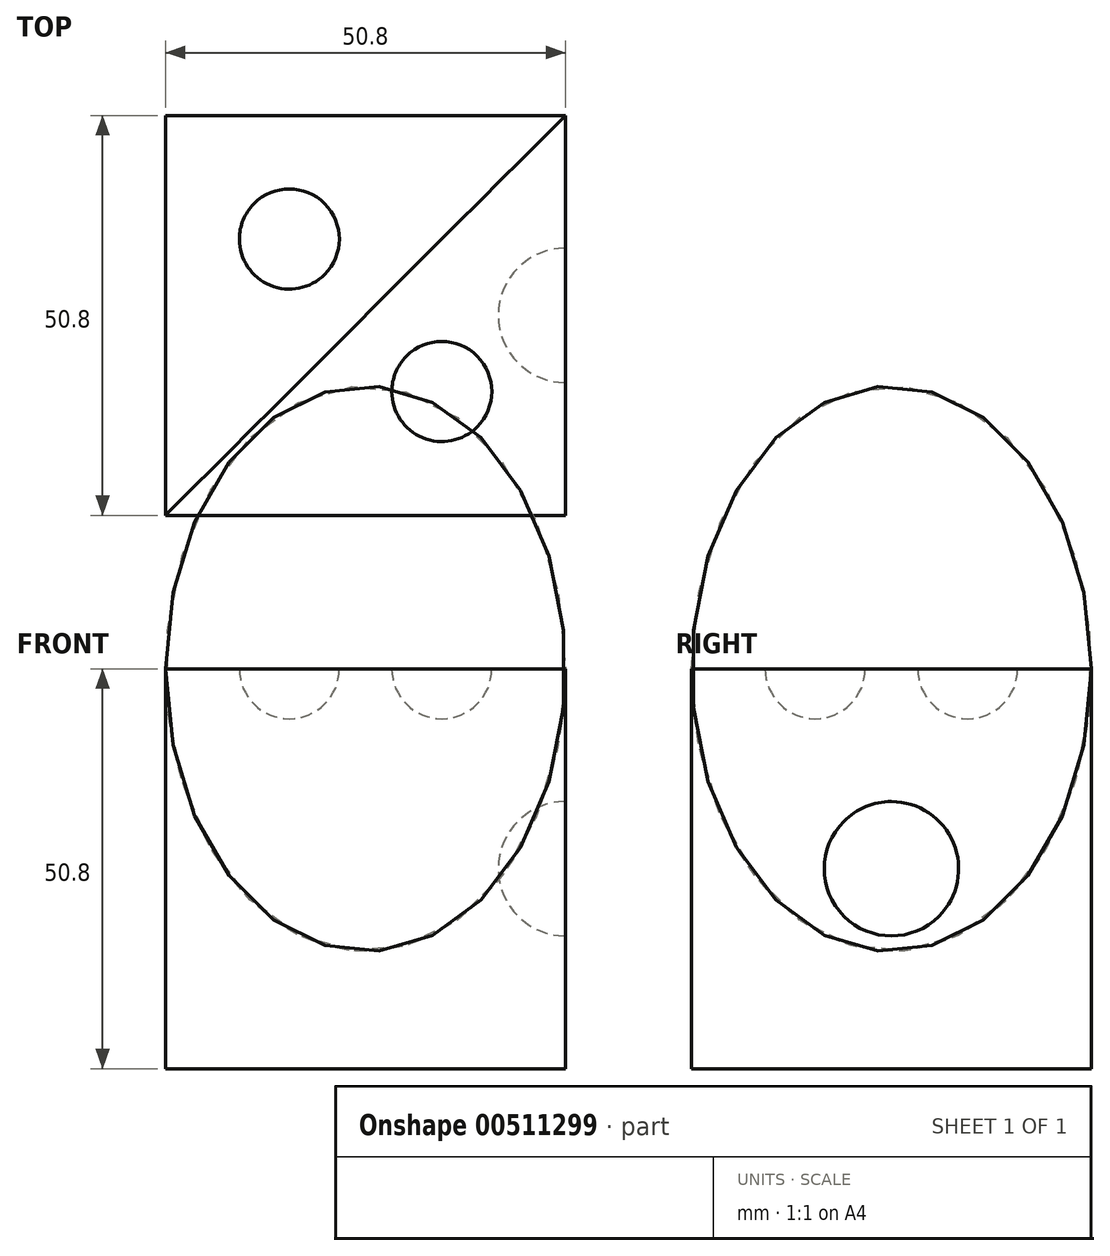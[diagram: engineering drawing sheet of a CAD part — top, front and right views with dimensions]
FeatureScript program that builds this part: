
annotation { "Feature Type Name" : "Feature", "Feature Type Description" : "" }
export const myFeature = defineFeature(function(context is Context, id is Id, definition is map)
    precondition{}
    {
        {
            var Q0;
            Q0=qCreatedBy(makeId("Front.planeOp"),FACE);
            var sketch = newSketch(context, id + "F0", { "sketchPlane" : qUnion([Q0])});
            skLineSegment(sketch, "E0", {"start": v(0, 0) * mm, "end": v(0, 50.8) * mm});
            skLineSegment(sketch, "E1", {"start": v(0, 0) * mm, "end": v(-50.8, 0) * mm});
            skLineSegment(sketch, "E2", {"start": v(0, 50.8) * mm, "end": v(-50.8, 50.8) * mm});
            skLineSegment(sketch, "E3", {"start": v(-50.8, 50.8) * mm, "end": v(-50.8, 0) * mm});
            skSolve(sketch);
        }
        {
            var Q0;
            Q0=makeQuery(id+"F0.imprint","IMPRINT",FACE,{"disambiguationData":[TD([[makeQuery(id+"F0.imprint","IMPRINT",EDGE,{"derivedFrom":sQuery(id+"F0.wireOp",EDGE,"E0")}),1.0]])]});
            extrude(context, id + "F1", {"entities" : qUnion([Q0]), "depth" : 50.8 * mm, "offsetDistance" : 25.4 * mm});
        }
        {
            var Q0;
            Q0=makeQuery(id+"F1.opExtrude","SWEPT_FACE",FACE,{"disambiguationData":[OSD([sQuery(id+"F0.wireOp",EDGE,"E0")])]});
            var sketch = newSketch(context, id + "F2", { "sketchPlane" : qUnion([Q0])});
            skCircle(sketch, "E4", {"center": v(-25.4, 25.4) * mm, "radius": 8.54 * mm});
            skPoint(sketch, "E5.orphan", {"position": v(-50.8, 50.8) * mm});
            skPoint(sketch, "E6.end.orphan", {"position": v(0, 0) * mm});
            skLineSegment(sketch, "E7", {"start": v(-53.06, 50.8) * mm, "end": v(-50.8, 50.8) * mm});
            skLineSegment(sketch, "E8", {"start": v(-50.8, 50.8) * mm, "end": v(0, 0) * mm});
            skSolve(sketch);
        }
        {
            var Q0;
            {var subQ0=sQuery(id+"F2.wireOp",EDGE,"E8");var subQ1=sQuery(id+"F2.wireOp",EDGE,"E4");var subQ2=makeQuery(id+"F2.imprint","INTERSECT",VERTEX,{"disambiguationData":[OD(0.0)],"derivedFrom":[subQ1,subQ0]});Q0=makeQuery(id+"F2.imprint","IMPRINT",FACE,{"disambiguationData":[TD([[makeQuery(id+"F2.imprint","IMPRINT",EDGE,{"disambiguationData":[TD([[subQ2,-1.0]])],"derivedFrom":subQ1}),1.0]])]});}
            var Q1;
            Q1=sQuery(id+"F2.wireOp",EDGE,"E8");
            revolve(context, id + "F3", {"operationType" : NewBodyOperationType.REMOVE, "entities" : qUnion([Q0]), "axis" : qUnion([Q1]), "revolveType" : RevolveType.FULL, "oppositeDirection" : true});
        }
        {
            var Q0;
            Q0=makeQuery(id+"F1.opExtrude","SWEPT_FACE",FACE,{"disambiguationData":[OSD([sQuery(id+"F0.wireOp",EDGE,"E2")])]});
            var sketch = newSketch(context, id + "F4", { "sketchPlane" : qUnion([Q0])});
            skLineSegment(sketch, "E9", {"start": v(-50.8, 0) * mm, "end": v(0, -50.8) * mm});
            skCircle(sketch, "E10", {"center": v(-35.08, -15.72) * mm, "radius": 6.35 * mm});
            skCircle(sketch, "E11", {"center": v(-15.72, -35.08) * mm, "radius": 6.35 * mm});
            skSolve(sketch);
        }
        {
            var Q0;
            {var subQ0=sQuery(id+"F4.wireOp",EDGE,"E10");var subQ1=sQuery(id+"F4.wireOp",EDGE,"E9");var subQ2=makeQuery(id+"F4.imprint","INTERSECT",VERTEX,{"disambiguationData":[OD(0.0)],"derivedFrom":[subQ1,subQ0]});Q0=makeQuery(id+"F4.imprint","IMPRINT",FACE,{"disambiguationData":[TD([[makeQuery(id+"F4.imprint","IMPRINT",EDGE,{"disambiguationData":[TD([[subQ2,-1.0]])],"derivedFrom":subQ1}),1.0]])]});}
            var Q1;
            {var subQ0=sQuery(id+"F4.wireOp",EDGE,"E11");var subQ1=sQuery(id+"F4.wireOp",EDGE,"E9");var subQ2=makeQuery(id+"F4.imprint","INTERSECT",VERTEX,{"disambiguationData":[OD(0.0)],"derivedFrom":[subQ1,subQ0]});Q1=makeQuery(id+"F4.imprint","IMPRINT",FACE,{"disambiguationData":[TD([[makeQuery(id+"F4.imprint","IMPRINT",EDGE,{"disambiguationData":[TD([[subQ2,-1.0]])],"derivedFrom":subQ1}),1.0]])]});}
            var Q2;
            Q2=sQuery(id+"F4.wireOp",EDGE,"E9");
            revolve(context, id + "F5", {"operationType" : NewBodyOperationType.REMOVE, "entities" : qUnion([Q0, Q1]), "axis" : qUnion([Q2]), "revolveType" : RevolveType.FULL});
        }
    });
